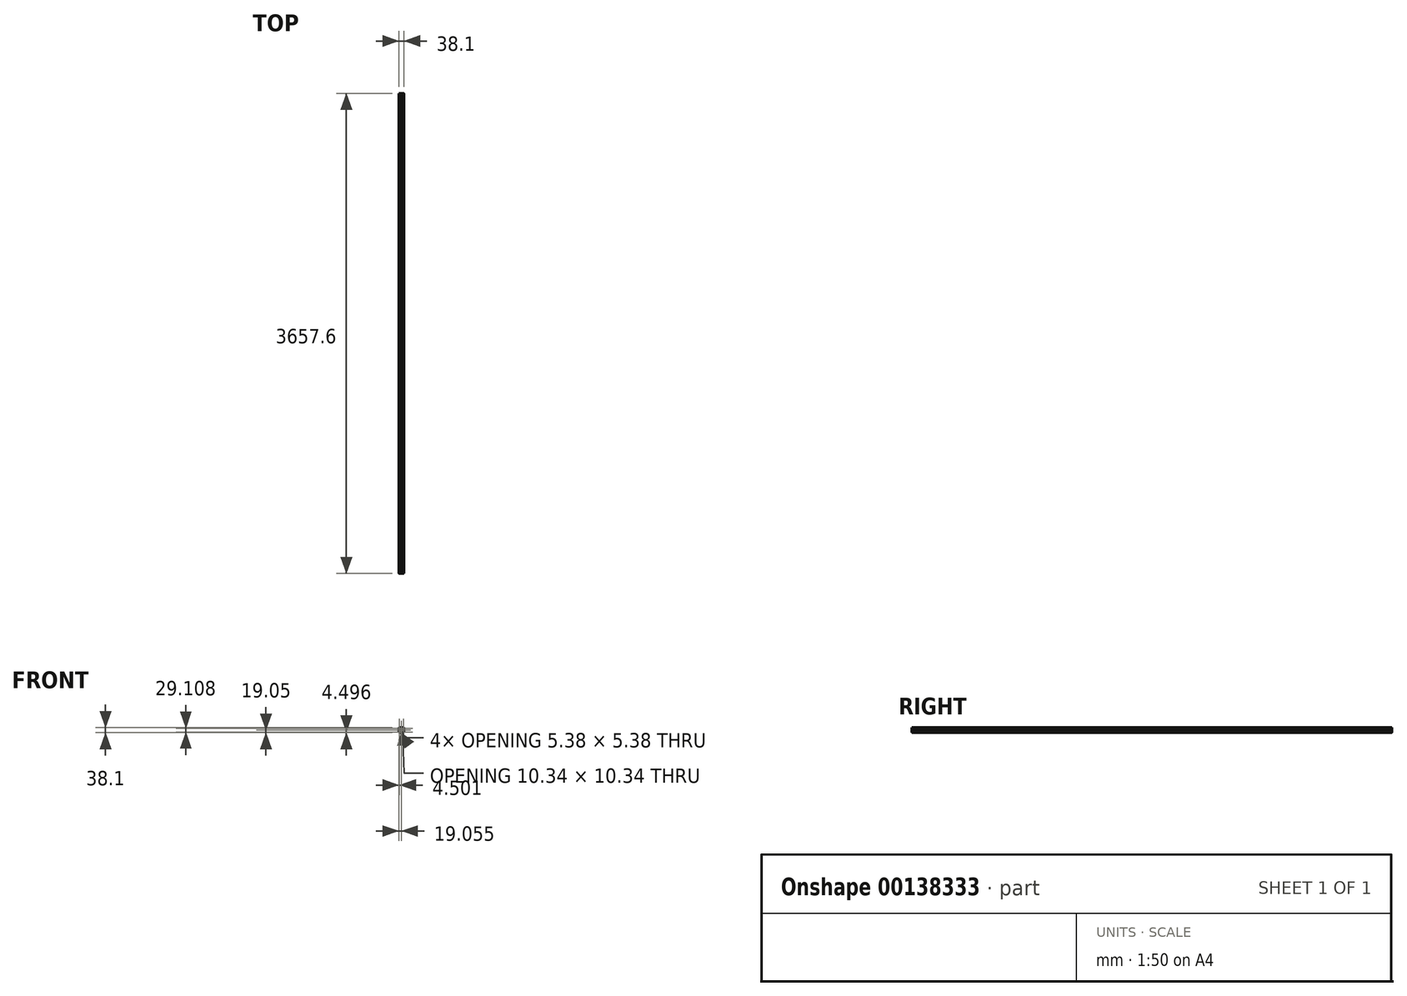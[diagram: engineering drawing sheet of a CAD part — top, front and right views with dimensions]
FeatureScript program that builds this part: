
annotation { "Feature Type Name" : "Feature", "Feature Type Description" : "" }
export const myFeature = defineFeature(function(context is Context, id is Id, definition is map)
    precondition{}
    {
        {
            var Q0;
            Q0=qCreatedBy(makeId("Front.planeOp"),FACE);
            var sketch = newSketch(context, id + "F0", { "sketchPlane" : qUnion([Q0])});
            skLineSegment(sketch, "E0", {"start": v(-126.4, 59.55) * mm, "end": v(-126.4, 54.72) * mm});
            skArc(sketch, "E1", {"start": v(-126.4, 53.2) * mm, "mid": v(-125.63, 53.96) * mm, "end": v(-126.4, 54.72) * mm});
            skArc(sketch, "E2", {"start": v(-126.4, 53.2) * mm, "mid": v(-125.47, 50.93) * mm, "end": v(-123.2, 50) * mm});
            skArc(sketch, "E3", {"start": v(-121.67, 50) * mm, "mid": v(-122.43, 50.76) * mm, "end": v(-123.2, 50) * mm});
            skLineSegment(sketch, "E4", {"start": v(-121.67, 50) * mm, "end": v(-116.84, 50) * mm});
            skArc(sketch, "E5", {"start": v(-115.32, 50) * mm, "mid": v(-116.08, 50.76) * mm, "end": v(-116.84, 50) * mm});
            skLineSegment(sketch, "E6", {"start": v(-115.32, 50) * mm, "end": v(-112.98, 50) * mm});
            skArc(sketch, "E7", {"start": v(-112.98, 50) * mm, "mid": v(-111.87, 50.46) * mm, "end": v(-111.4, 51.57) * mm});
            skLineSegment(sketch, "E8", {"start": v(-111.4, 51.57) * mm, "end": v(-111.4, 52.49) * mm});
            skArc(sketch, "E9", {"start": v(-111.4, 52.49) * mm, "mid": v(-111.87, 53.6) * mm, "end": v(-112.98, 54.06) * mm});
            skLineSegment(sketch, "E10", {"start": v(-112.98, 54.06) * mm, "end": v(-113.7, 54.06) * mm});
            skArc(sketch, "E11", {"start": v(-113.7, 54.06) * mm, "mid": v(-113.96, 53.95) * mm, "end": v(-114.08, 53.68) * mm});
            skLineSegment(sketch, "E12", {"start": v(-114.08, 53.68) * mm, "end": v(-114.08, 53.35) * mm});
            skArc(sketch, "E13", {"start": v(-114.46, 52.97) * mm, "mid": v(-114.19, 53.08) * mm, "end": v(-114.08, 53.35) * mm});
            skLineSegment(sketch, "E14", {"start": v(-114.46, 52.97) * mm, "end": v(-116.74, 52.97) * mm});
            skArc(sketch, "E15", {"start": v(-117.63, 53.86) * mm, "mid": v(-117.37, 53.23) * mm, "end": v(-116.74, 52.97) * mm});
            skLineSegment(sketch, "E16", {"start": v(-117.63, 53.86) * mm, "end": v(-117.63, 56.67) * mm});
            skArc(sketch, "E17", {"start": v(-117.26, 57.57) * mm, "mid": v(-117.54, 57.16) * mm, "end": v(-117.63, 56.67) * mm});
            skLineSegment(sketch, "E18", {"start": v(-117.26, 57.57) * mm, "end": v(-112.9, 61.93) * mm});
            skArc(sketch, "E19", {"start": v(-112, 62.3) * mm, "mid": v(-112.49, 62.2) * mm, "end": v(-112.9, 61.93) * mm});
            skLineSegment(sketch, "E20", {"start": v(-112, 62.3) * mm, "end": v(-102.7, 62.3) * mm});
            skArc(sketch, "E21", {"start": v(-101.8, 61.93) * mm, "mid": v(-102.2, 62.2) * mm, "end": v(-102.7, 62.3) * mm});
            skLineSegment(sketch, "E22", {"start": v(-101.8, 61.93) * mm, "end": v(-97.43, 57.57) * mm});
            skArc(sketch, "E23", {"start": v(-97.06, 56.67) * mm, "mid": v(-97.15, 57.16) * mm, "end": v(-97.43, 57.57) * mm});
            skLineSegment(sketch, "E24", {"start": v(-97.06, 56.67) * mm, "end": v(-97.06, 53.86) * mm});
            skArc(sketch, "E25", {"start": v(-97.95, 52.97) * mm, "mid": v(-97.32, 53.23) * mm, "end": v(-97.06, 53.86) * mm});
            skLineSegment(sketch, "E26", {"start": v(-97.95, 52.97) * mm, "end": v(-100.23, 52.97) * mm});
            skArc(sketch, "E27", {"start": v(-100.61, 53.35) * mm, "mid": v(-100.5, 53.08) * mm, "end": v(-100.23, 52.97) * mm});
            skLineSegment(sketch, "E28", {"start": v(-100.61, 53.35) * mm, "end": v(-100.61, 53.68) * mm});
            skArc(sketch, "E29", {"start": v(-100.61, 53.68) * mm, "mid": v(-100.73, 53.95) * mm, "end": v(-101, 54.06) * mm});
            skLineSegment(sketch, "E30", {"start": v(-101, 54.06) * mm, "end": v(-101.7, 54.06) * mm});
            skArc(sketch, "E31", {"start": v(-101.7, 54.06) * mm, "mid": v(-102.82, 53.6) * mm, "end": v(-103.28, 52.49) * mm});
            skLineSegment(sketch, "E32", {"start": v(-103.28, 52.49) * mm, "end": v(-103.28, 51.57) * mm});
            skArc(sketch, "E33", {"start": v(-103.28, 51.57) * mm, "mid": v(-102.82, 50.46) * mm, "end": v(-101.7, 50) * mm});
            skLineSegment(sketch, "E34", {"start": v(-101.7, 50) * mm, "end": v(-99.37, 50) * mm});
            skArc(sketch, "E35", {"start": v(-97.85, 50) * mm, "mid": v(-98.6, 50.76) * mm, "end": v(-99.37, 50) * mm});
            skLineSegment(sketch, "E36", {"start": v(-97.85, 50) * mm, "end": v(-93.02, 50) * mm});
            skArc(sketch, "E37", {"start": v(-91.5, 50) * mm, "mid": v(-92.26, 50.76) * mm, "end": v(-93.02, 50) * mm});
            skArc(sketch, "E38", {"start": v(-91.5, 50) * mm, "mid": v(-89.23, 50.93) * mm, "end": v(-88.3, 53.2) * mm});
            skArc(sketch, "E39", {"start": v(-88.3, 54.72) * mm, "mid": v(-89.06, 53.96) * mm, "end": v(-88.3, 53.2) * mm});
            skLineSegment(sketch, "E40", {"start": v(-88.3, 54.72) * mm, "end": v(-88.3, 59.55) * mm});
            skArc(sketch, "E41", {"start": v(-88.3, 61.07) * mm, "mid": v(-89.06, 60.31) * mm, "end": v(-88.3, 59.55) * mm});
            skLineSegment(sketch, "E42", {"start": v(-88.3, 61.07) * mm, "end": v(-88.3, 63.41) * mm});
            skArc(sketch, "E43", {"start": v(-88.3, 63.41) * mm, "mid": v(-88.76, 64.52) * mm, "end": v(-89.87, 64.99) * mm});
            skLineSegment(sketch, "E44", {"start": v(-89.87, 64.99) * mm, "end": v(-90.78, 64.99) * mm});
            skArc(sketch, "E45", {"start": v(-90.78, 64.99) * mm, "mid": v(-91.9, 64.52) * mm, "end": v(-92.36, 63.41) * mm});
            skLineSegment(sketch, "E46", {"start": v(-92.36, 63.41) * mm, "end": v(-92.36, 62.7) * mm});
            skArc(sketch, "E47", {"start": v(-92.36, 62.7) * mm, "mid": v(-92.25, 62.43) * mm, "end": v(-91.98, 62.32) * mm});
            skLineSegment(sketch, "E48", {"start": v(-91.98, 62.32) * mm, "end": v(-91.65, 62.32) * mm});
            skArc(sketch, "E49", {"start": v(-91.27, 61.94) * mm, "mid": v(-91.38, 62.2) * mm, "end": v(-91.65, 62.32) * mm});
            skLineSegment(sketch, "E50", {"start": v(-91.27, 61.94) * mm, "end": v(-91.27, 59.65) * mm});
            skArc(sketch, "E51", {"start": v(-92.16, 58.76) * mm, "mid": v(-91.53, 59.02) * mm, "end": v(-91.27, 59.65) * mm});
            skLineSegment(sketch, "E52", {"start": v(-92.16, 58.76) * mm, "end": v(-94.97, 58.76) * mm});
            skArc(sketch, "E53", {"start": v(-95.87, 59.13) * mm, "mid": v(-95.46, 58.86) * mm, "end": v(-94.97, 58.76) * mm});
            skLineSegment(sketch, "E54", {"start": v(-95.87, 59.13) * mm, "end": v(-100.23, 63.5) * mm});
            skArc(sketch, "E55", {"start": v(-100.6, 64.4) * mm, "mid": v(-100.5, 63.9) * mm, "end": v(-100.23, 63.5) * mm});
            skLineSegment(sketch, "E56", {"start": v(-100.6, 64.4) * mm, "end": v(-100.6, 73.7) * mm});
            skArc(sketch, "E57", {"start": v(-100.23, 74.6) * mm, "mid": v(-100.5, 74.2) * mm, "end": v(-100.6, 73.7) * mm});
            skLineSegment(sketch, "E58", {"start": v(-100.23, 74.6) * mm, "end": v(-95.87, 78.96) * mm});
            skArc(sketch, "E59", {"start": v(-94.97, 79.34) * mm, "mid": v(-95.46, 79.24) * mm, "end": v(-95.87, 78.96) * mm});
            skLineSegment(sketch, "E60", {"start": v(-94.97, 79.34) * mm, "end": v(-92.16, 79.34) * mm});
            skArc(sketch, "E61", {"start": v(-91.27, 78.45) * mm, "mid": v(-91.53, 79.08) * mm, "end": v(-92.16, 79.34) * mm});
            skLineSegment(sketch, "E62", {"start": v(-91.27, 78.45) * mm, "end": v(-91.27, 76.16) * mm});
            skArc(sketch, "E63", {"start": v(-91.65, 75.78) * mm, "mid": v(-91.38, 75.9) * mm, "end": v(-91.27, 76.16) * mm});
            skLineSegment(sketch, "E64", {"start": v(-91.65, 75.78) * mm, "end": v(-91.98, 75.78) * mm});
            skArc(sketch, "E65", {"start": v(-91.98, 75.78) * mm, "mid": v(-92.25, 75.67) * mm, "end": v(-92.36, 75.4) * mm});
            skLineSegment(sketch, "E66", {"start": v(-92.36, 75.4) * mm, "end": v(-92.36, 74.69) * mm});
            skArc(sketch, "E67", {"start": v(-92.36, 74.69) * mm, "mid": v(-91.9, 73.58) * mm, "end": v(-90.78, 73.11) * mm});
            skLineSegment(sketch, "E68", {"start": v(-90.78, 73.11) * mm, "end": v(-89.87, 73.11) * mm});
            skArc(sketch, "E69", {"start": v(-89.87, 73.11) * mm, "mid": v(-88.76, 73.58) * mm, "end": v(-88.3, 74.69) * mm});
            skLineSegment(sketch, "E70", {"start": v(-88.3, 74.69) * mm, "end": v(-88.3, 77.03) * mm});
            skArc(sketch, "E71", {"start": v(-88.3, 78.55) * mm, "mid": v(-89.06, 77.79) * mm, "end": v(-88.3, 77.03) * mm});
            skLineSegment(sketch, "E72", {"start": v(-88.3, 78.55) * mm, "end": v(-88.3, 83.38) * mm});
            skArc(sketch, "E73", {"start": v(-88.3, 84.9) * mm, "mid": v(-89.06, 84.14) * mm, "end": v(-88.3, 83.38) * mm});
            skArc(sketch, "E74", {"start": v(-88.3, 84.9) * mm, "mid": v(-89.23, 87.17) * mm, "end": v(-91.5, 88.1) * mm});
            skArc(sketch, "E75", {"start": v(-93.02, 88.1) * mm, "mid": v(-92.26, 87.34) * mm, "end": v(-91.5, 88.1) * mm});
            skLineSegment(sketch, "E76", {"start": v(-93.02, 88.1) * mm, "end": v(-97.85, 88.1) * mm});
            skArc(sketch, "E77", {"start": v(-99.37, 88.1) * mm, "mid": v(-98.6, 87.34) * mm, "end": v(-97.85, 88.1) * mm});
            skLineSegment(sketch, "E78", {"start": v(-99.37, 88.1) * mm, "end": v(-101.7, 88.1) * mm});
            skArc(sketch, "E79", {"start": v(-101.7, 88.1) * mm, "mid": v(-102.82, 87.64) * mm, "end": v(-103.28, 86.53) * mm});
            skLineSegment(sketch, "E80", {"start": v(-103.28, 86.53) * mm, "end": v(-103.28, 85.61) * mm});
            skArc(sketch, "E81", {"start": v(-103.28, 85.61) * mm, "mid": v(-102.82, 84.5) * mm, "end": v(-101.7, 84.04) * mm});
            skLineSegment(sketch, "E82", {"start": v(-101.7, 84.04) * mm, "end": v(-101, 84.04) * mm});
            skArc(sketch, "E83", {"start": v(-101, 84.04) * mm, "mid": v(-100.73, 84.15) * mm, "end": v(-100.61, 84.42) * mm});
            skLineSegment(sketch, "E84", {"start": v(-100.61, 84.42) * mm, "end": v(-100.61, 84.75) * mm});
            skArc(sketch, "E85", {"start": v(-100.23, 85.13) * mm, "mid": v(-100.5, 85.02) * mm, "end": v(-100.61, 84.75) * mm});
            skLineSegment(sketch, "E86", {"start": v(-100.23, 85.13) * mm, "end": v(-97.95, 85.13) * mm});
            skArc(sketch, "E87", {"start": v(-97.06, 84.24) * mm, "mid": v(-97.32, 84.87) * mm, "end": v(-97.95, 85.13) * mm});
            skLineSegment(sketch, "E88", {"start": v(-97.06, 84.24) * mm, "end": v(-97.06, 81.43) * mm});
            skArc(sketch, "E89", {"start": v(-97.43, 80.53) * mm, "mid": v(-97.15, 80.94) * mm, "end": v(-97.06, 81.43) * mm});
            skLineSegment(sketch, "E90", {"start": v(-97.43, 80.53) * mm, "end": v(-101.8, 76.17) * mm});
            skArc(sketch, "E91", {"start": v(-102.7, 75.8) * mm, "mid": v(-102.2, 75.9) * mm, "end": v(-101.8, 76.17) * mm});
            skLineSegment(sketch, "E92", {"start": v(-102.7, 75.8) * mm, "end": v(-112, 75.8) * mm});
            skArc(sketch, "E93", {"start": v(-112.9, 76.17) * mm, "mid": v(-112.49, 75.9) * mm, "end": v(-112, 75.8) * mm});
            skLineSegment(sketch, "E94", {"start": v(-112.9, 76.17) * mm, "end": v(-117.26, 80.53) * mm});
            skArc(sketch, "E95", {"start": v(-117.63, 81.43) * mm, "mid": v(-117.54, 80.94) * mm, "end": v(-117.26, 80.53) * mm});
            skLineSegment(sketch, "E96", {"start": v(-117.63, 81.43) * mm, "end": v(-117.63, 84.24) * mm});
            skArc(sketch, "E97", {"start": v(-116.74, 85.13) * mm, "mid": v(-117.37, 84.87) * mm, "end": v(-117.63, 84.24) * mm});
            skLineSegment(sketch, "E98", {"start": v(-116.74, 85.13) * mm, "end": v(-114.46, 85.13) * mm});
            skArc(sketch, "E99", {"start": v(-114.08, 84.75) * mm, "mid": v(-114.19, 85.02) * mm, "end": v(-114.46, 85.13) * mm});
            skLineSegment(sketch, "E100", {"start": v(-114.08, 84.75) * mm, "end": v(-114.08, 84.42) * mm});
            skArc(sketch, "E101", {"start": v(-114.08, 84.42) * mm, "mid": v(-113.96, 84.15) * mm, "end": v(-113.7, 84.04) * mm});
            skLineSegment(sketch, "E102", {"start": v(-113.7, 84.04) * mm, "end": v(-112.98, 84.04) * mm});
            skArc(sketch, "E103", {"start": v(-112.98, 84.04) * mm, "mid": v(-111.87, 84.5) * mm, "end": v(-111.4, 85.61) * mm});
            skLineSegment(sketch, "E104", {"start": v(-111.4, 85.61) * mm, "end": v(-111.4, 86.53) * mm});
            skArc(sketch, "E105", {"start": v(-111.4, 86.53) * mm, "mid": v(-111.87, 87.64) * mm, "end": v(-112.98, 88.1) * mm});
            skLineSegment(sketch, "E106", {"start": v(-112.98, 88.1) * mm, "end": v(-115.32, 88.1) * mm});
            skArc(sketch, "E107", {"start": v(-116.84, 88.1) * mm, "mid": v(-116.08, 87.34) * mm, "end": v(-115.32, 88.1) * mm});
            skLineSegment(sketch, "E108", {"start": v(-116.84, 88.1) * mm, "end": v(-121.67, 88.1) * mm});
            skArc(sketch, "E109", {"start": v(-123.2, 88.1) * mm, "mid": v(-122.43, 87.34) * mm, "end": v(-121.67, 88.1) * mm});
            skArc(sketch, "E110", {"start": v(-123.2, 88.1) * mm, "mid": v(-125.47, 87.17) * mm, "end": v(-126.4, 84.9) * mm});
            skArc(sketch, "E111", {"start": v(-126.4, 83.38) * mm, "mid": v(-125.63, 84.14) * mm, "end": v(-126.4, 84.9) * mm});
            skLineSegment(sketch, "E112", {"start": v(-126.4, 83.38) * mm, "end": v(-126.4, 78.55) * mm});
            skArc(sketch, "E113", {"start": v(-126.4, 77.03) * mm, "mid": v(-125.63, 77.79) * mm, "end": v(-126.4, 78.55) * mm});
            skLineSegment(sketch, "E114", {"start": v(-126.4, 77.03) * mm, "end": v(-126.4, 74.69) * mm});
            skArc(sketch, "E115", {"start": v(-126.4, 74.69) * mm, "mid": v(-125.93, 73.58) * mm, "end": v(-124.82, 73.11) * mm});
            skLineSegment(sketch, "E116", {"start": v(-124.82, 73.11) * mm, "end": v(-123.9, 73.11) * mm});
            skArc(sketch, "E117", {"start": v(-123.9, 73.11) * mm, "mid": v(-122.8, 73.58) * mm, "end": v(-122.33, 74.69) * mm});
            skLineSegment(sketch, "E118", {"start": v(-122.33, 74.69) * mm, "end": v(-122.33, 75.4) * mm});
            skArc(sketch, "E119", {"start": v(-122.33, 75.4) * mm, "mid": v(-122.44, 75.67) * mm, "end": v(-122.71, 75.78) * mm});
            skLineSegment(sketch, "E120", {"start": v(-122.71, 75.78) * mm, "end": v(-123.04, 75.78) * mm});
            skArc(sketch, "E121", {"start": v(-123.42, 76.16) * mm, "mid": v(-123.31, 75.9) * mm, "end": v(-123.04, 75.78) * mm});
            skLineSegment(sketch, "E122", {"start": v(-123.42, 76.16) * mm, "end": v(-123.42, 78.45) * mm});
            skArc(sketch, "E123", {"start": v(-122.53, 79.34) * mm, "mid": v(-123.16, 79.08) * mm, "end": v(-123.42, 78.45) * mm});
            skLineSegment(sketch, "E124", {"start": v(-122.53, 79.34) * mm, "end": v(-119.72, 79.34) * mm});
            skArc(sketch, "E125", {"start": v(-118.82, 78.96) * mm, "mid": v(-119.23, 79.24) * mm, "end": v(-119.72, 79.34) * mm});
            skLineSegment(sketch, "E126", {"start": v(-118.82, 78.96) * mm, "end": v(-114.46, 74.6) * mm});
            skArc(sketch, "E127", {"start": v(-114.09, 73.7) * mm, "mid": v(-114.19, 74.2) * mm, "end": v(-114.46, 74.6) * mm});
            skLineSegment(sketch, "E128", {"start": v(-114.09, 73.7) * mm, "end": v(-114.09, 64.4) * mm});
            skArc(sketch, "E129", {"start": v(-114.46, 63.5) * mm, "mid": v(-114.19, 63.9) * mm, "end": v(-114.09, 64.4) * mm});
            skLineSegment(sketch, "E130", {"start": v(-114.46, 63.5) * mm, "end": v(-118.82, 59.13) * mm});
            skArc(sketch, "E131", {"start": v(-119.72, 58.76) * mm, "mid": v(-119.23, 58.86) * mm, "end": v(-118.82, 59.13) * mm});
            skLineSegment(sketch, "E132", {"start": v(-119.72, 58.76) * mm, "end": v(-122.53, 58.76) * mm});
            skArc(sketch, "E133", {"start": v(-123.42, 59.65) * mm, "mid": v(-123.16, 59.02) * mm, "end": v(-122.53, 58.76) * mm});
            skLineSegment(sketch, "E134", {"start": v(-123.42, 59.65) * mm, "end": v(-123.42, 61.94) * mm});
            skArc(sketch, "E135", {"start": v(-123.04, 62.32) * mm, "mid": v(-123.31, 62.2) * mm, "end": v(-123.42, 61.94) * mm});
            skLineSegment(sketch, "E136", {"start": v(-123.04, 62.32) * mm, "end": v(-122.71, 62.32) * mm});
            skArc(sketch, "E137", {"start": v(-122.71, 62.32) * mm, "mid": v(-122.44, 62.43) * mm, "end": v(-122.33, 62.7) * mm});
            skLineSegment(sketch, "E138", {"start": v(-122.33, 62.7) * mm, "end": v(-122.33, 63.41) * mm});
            skArc(sketch, "E139", {"start": v(-122.33, 63.41) * mm, "mid": v(-122.8, 64.52) * mm, "end": v(-123.9, 64.99) * mm});
            skLineSegment(sketch, "E140", {"start": v(-123.9, 64.99) * mm, "end": v(-124.82, 64.99) * mm});
            skArc(sketch, "E141", {"start": v(-124.82, 64.99) * mm, "mid": v(-125.93, 64.52) * mm, "end": v(-126.4, 63.41) * mm});
            skLineSegment(sketch, "E142", {"start": v(-126.4, 63.41) * mm, "end": v(-126.4, 61.07) * mm});
            skArc(sketch, "E143", {"start": v(-95.1, 86.3) * mm, "mid": v(-95.37, 86.18) * mm, "end": v(-95.48, 85.92) * mm});
            skLineSegment(sketch, "E144", {"start": v(-92.9, 86.3) * mm, "end": v(-95.1, 86.3) * mm});
            skArc(sketch, "E145", {"start": v(-90.1, 83.5) * mm, "mid": v(-90.92, 85.48) * mm, "end": v(-92.9, 86.3) * mm});
            skLineSegment(sketch, "E146", {"start": v(-90.1, 81.3) * mm, "end": v(-90.1, 83.5) * mm});
            skArc(sketch, "E147", {"start": v(-90.48, 80.91) * mm, "mid": v(-90.21, 81.02) * mm, "end": v(-90.1, 81.3) * mm});
            skLineSegment(sketch, "E148", {"start": v(-92.25, 80.91) * mm, "end": v(-90.48, 80.91) * mm});
            skLineSegment(sketch, "E149", {"start": v(-92.8, 81.45) * mm, "end": v(-92.25, 80.91) * mm});
            skLineSegment(sketch, "E150", {"start": v(-93.33, 80.91) * mm, "end": v(-92.8, 81.45) * mm});
            skLineSegment(sketch, "E151", {"start": v(-95.1, 80.91) * mm, "end": v(-93.33, 80.91) * mm});
            skArc(sketch, "E152", {"start": v(-95.48, 81.3) * mm, "mid": v(-95.37, 81.02) * mm, "end": v(-95.1, 80.91) * mm});
            skLineSegment(sketch, "E153", {"start": v(-95.48, 83.07) * mm, "end": v(-95.48, 81.3) * mm});
            skLineSegment(sketch, "E154", {"start": v(-94.94, 83.6) * mm, "end": v(-95.48, 83.07) * mm});
            skLineSegment(sketch, "E155", {"start": v(-95.48, 84.14) * mm, "end": v(-94.94, 83.6) * mm});
            skLineSegment(sketch, "E156", {"start": v(-95.48, 56.8) * mm, "end": v(-95.48, 55.03) * mm});
            skArc(sketch, "E157", {"start": v(-95.1, 57.19) * mm, "mid": v(-95.37, 57.08) * mm, "end": v(-95.48, 56.8) * mm});
            skLineSegment(sketch, "E158", {"start": v(-93.33, 57.19) * mm, "end": v(-95.1, 57.19) * mm});
            skLineSegment(sketch, "E159", {"start": v(-92.8, 56.65) * mm, "end": v(-93.33, 57.19) * mm});
            skLineSegment(sketch, "E160", {"start": v(-92.25, 57.19) * mm, "end": v(-92.8, 56.65) * mm});
            skLineSegment(sketch, "E161", {"start": v(-90.48, 57.19) * mm, "end": v(-92.25, 57.19) * mm});
            skArc(sketch, "E162", {"start": v(-90.1, 56.8) * mm, "mid": v(-90.21, 57.08) * mm, "end": v(-90.48, 57.19) * mm});
            skLineSegment(sketch, "E163", {"start": v(-90.1, 54.6) * mm, "end": v(-90.1, 56.8) * mm});
            skArc(sketch, "E164", {"start": v(-92.9, 51.8) * mm, "mid": v(-90.92, 52.62) * mm, "end": v(-90.1, 54.6) * mm});
            skLineSegment(sketch, "E165", {"start": v(-95.1, 51.8) * mm, "end": v(-92.9, 51.8) * mm});
            skArc(sketch, "E166", {"start": v(-95.48, 52.18) * mm, "mid": v(-95.37, 51.91) * mm, "end": v(-95.1, 51.8) * mm});
            skLineSegment(sketch, "E167", {"start": v(-95.48, 53.96) * mm, "end": v(-95.48, 52.18) * mm});
            skLineSegment(sketch, "E168", {"start": v(-94.94, 54.5) * mm, "end": v(-95.48, 53.96) * mm});
            skLineSegment(sketch, "E169", {"start": v(-112.51, 65.13) * mm, "end": v(-112.51, 64.14) * mm});
            skArc(sketch, "E170", {"start": v(-112.25, 65.76) * mm, "mid": v(-112.45, 65.47) * mm, "end": v(-112.51, 65.13) * mm});
            skLineSegment(sketch, "E171", {"start": v(-110.54, 67.47) * mm, "end": v(-112.25, 65.76) * mm});
            skArc(sketch, "E172", {"start": v(-110.54, 67.47) * mm, "mid": v(-110.44, 67.66) * mm, "end": v(-110.46, 67.87) * mm});
            skArc(sketch, "E173", {"start": v(-110.46, 70.23) * mm, "mid": v(-110.67, 69.05) * mm, "end": v(-110.46, 67.87) * mm});
            skArc(sketch, "E174", {"start": v(-110.46, 70.23) * mm, "mid": v(-110.44, 70.44) * mm, "end": v(-110.54, 70.63) * mm});
            skLineSegment(sketch, "E175", {"start": v(-112.25, 72.34) * mm, "end": v(-110.54, 70.63) * mm});
            skArc(sketch, "E176", {"start": v(-112.51, 72.97) * mm, "mid": v(-112.45, 72.63) * mm, "end": v(-112.25, 72.34) * mm});
            skLineSegment(sketch, "E177", {"start": v(-112.51, 73.96) * mm, "end": v(-112.51, 72.97) * mm});
            skArc(sketch, "E178", {"start": v(-112.26, 74.22) * mm, "mid": v(-112.44, 74.14) * mm, "end": v(-112.51, 73.96) * mm});
            skLineSegment(sketch, "E179", {"start": v(-111.27, 74.22) * mm, "end": v(-112.26, 74.22) * mm});
            skArc(sketch, "E180", {"start": v(-110.64, 73.96) * mm, "mid": v(-110.93, 74.15) * mm, "end": v(-111.27, 74.22) * mm});
            skLineSegment(sketch, "E181", {"start": v(-108.93, 72.25) * mm, "end": v(-110.64, 73.96) * mm});
            skArc(sketch, "E182", {"start": v(-108.93, 72.25) * mm, "mid": v(-108.74, 72.15) * mm, "end": v(-108.52, 72.16) * mm});
            skArc(sketch, "E183", {"start": v(-106.17, 72.16) * mm, "mid": v(-107.35, 72.38) * mm, "end": v(-108.52, 72.16) * mm});
            skArc(sketch, "E184", {"start": v(-106.17, 72.16) * mm, "mid": v(-105.95, 72.15) * mm, "end": v(-105.76, 72.25) * mm});
            skLineSegment(sketch, "E185", {"start": v(-104.05, 73.96) * mm, "end": v(-105.76, 72.25) * mm});
            skArc(sketch, "E186", {"start": v(-103.42, 74.22) * mm, "mid": v(-103.76, 74.15) * mm, "end": v(-104.05, 73.96) * mm});
            skLineSegment(sketch, "E187", {"start": v(-102.43, 74.22) * mm, "end": v(-103.42, 74.22) * mm});
            skArc(sketch, "E188", {"start": v(-102.18, 73.96) * mm, "mid": v(-102.25, 74.14) * mm, "end": v(-102.43, 74.22) * mm});
            skLineSegment(sketch, "E189", {"start": v(-102.18, 72.97) * mm, "end": v(-102.18, 73.96) * mm});
            skArc(sketch, "E190", {"start": v(-102.44, 72.34) * mm, "mid": v(-102.24, 72.63) * mm, "end": v(-102.18, 72.97) * mm});
            skLineSegment(sketch, "E191", {"start": v(-104.15, 70.63) * mm, "end": v(-102.44, 72.34) * mm});
            skArc(sketch, "E192", {"start": v(-104.15, 70.63) * mm, "mid": v(-104.25, 70.44) * mm, "end": v(-104.23, 70.23) * mm});
            skArc(sketch, "E193", {"start": v(-104.23, 67.87) * mm, "mid": v(-104.02, 69.05) * mm, "end": v(-104.23, 70.23) * mm});
            skArc(sketch, "E194", {"start": v(-104.23, 67.87) * mm, "mid": v(-104.25, 67.66) * mm, "end": v(-104.15, 67.47) * mm});
            skLineSegment(sketch, "E195", {"start": v(-102.44, 65.76) * mm, "end": v(-104.15, 67.47) * mm});
            skArc(sketch, "E196", {"start": v(-102.18, 65.13) * mm, "mid": v(-102.24, 65.47) * mm, "end": v(-102.44, 65.76) * mm});
            skLineSegment(sketch, "E197", {"start": v(-102.18, 64.14) * mm, "end": v(-102.18, 65.13) * mm});
            skArc(sketch, "E198", {"start": v(-102.43, 63.88) * mm, "mid": v(-102.25, 63.96) * mm, "end": v(-102.18, 64.14) * mm});
            skLineSegment(sketch, "E199", {"start": v(-103.42, 63.88) * mm, "end": v(-102.43, 63.88) * mm});
            skArc(sketch, "E200", {"start": v(-104.05, 64.14) * mm, "mid": v(-103.76, 63.95) * mm, "end": v(-103.42, 63.88) * mm});
            skLineSegment(sketch, "E201", {"start": v(-105.76, 65.85) * mm, "end": v(-104.05, 64.14) * mm});
            skArc(sketch, "E202", {"start": v(-105.76, 65.85) * mm, "mid": v(-105.95, 65.95) * mm, "end": v(-106.17, 65.94) * mm});
            skArc(sketch, "E203", {"start": v(-108.52, 65.94) * mm, "mid": v(-107.35, 65.72) * mm, "end": v(-106.17, 65.94) * mm});
            skArc(sketch, "E204", {"start": v(-108.52, 65.94) * mm, "mid": v(-108.74, 65.95) * mm, "end": v(-108.93, 65.85) * mm});
            skLineSegment(sketch, "E205", {"start": v(-110.64, 64.14) * mm, "end": v(-108.93, 65.85) * mm});
            skArc(sketch, "E206", {"start": v(-111.27, 63.88) * mm, "mid": v(-110.93, 63.95) * mm, "end": v(-110.64, 64.14) * mm});
            skLineSegment(sketch, "E207", {"start": v(-112.26, 63.88) * mm, "end": v(-111.27, 63.88) * mm});
            skLineSegment(sketch, "E208", {"start": v(-124.6, 56.8) * mm, "end": v(-124.6, 54.6) * mm});
            skArc(sketch, "E209", {"start": v(-124.21, 57.19) * mm, "mid": v(-124.48, 57.08) * mm, "end": v(-124.6, 56.8) * mm});
            skLineSegment(sketch, "E210", {"start": v(-122.44, 57.19) * mm, "end": v(-124.21, 57.19) * mm});
            skLineSegment(sketch, "E211", {"start": v(-121.9, 56.65) * mm, "end": v(-122.44, 57.19) * mm});
            skLineSegment(sketch, "E212", {"start": v(-121.36, 57.19) * mm, "end": v(-121.9, 56.65) * mm});
            skLineSegment(sketch, "E213", {"start": v(-119.59, 57.19) * mm, "end": v(-121.36, 57.19) * mm});
            skArc(sketch, "E214", {"start": v(-119.2, 56.8) * mm, "mid": v(-119.32, 57.08) * mm, "end": v(-119.59, 57.19) * mm});
            skLineSegment(sketch, "E215", {"start": v(-119.2, 55.03) * mm, "end": v(-119.2, 56.8) * mm});
            skLineSegment(sketch, "E216", {"start": v(-119.75, 54.5) * mm, "end": v(-119.2, 55.03) * mm});
            skLineSegment(sketch, "E217", {"start": v(-119.2, 53.96) * mm, "end": v(-119.75, 54.5) * mm});
            skLineSegment(sketch, "E218", {"start": v(-119.2, 52.18) * mm, "end": v(-119.2, 53.96) * mm});
            skArc(sketch, "E219", {"start": v(-119.59, 51.8) * mm, "mid": v(-119.32, 51.91) * mm, "end": v(-119.2, 52.18) * mm});
            skLineSegment(sketch, "E220", {"start": v(-121.8, 51.8) * mm, "end": v(-119.59, 51.8) * mm});
            skLineSegment(sketch, "E221", {"start": v(-124.6, 83.5) * mm, "end": v(-124.6, 81.3) * mm});
            skArc(sketch, "E222", {"start": v(-121.8, 86.3) * mm, "mid": v(-123.77, 85.48) * mm, "end": v(-124.6, 83.5) * mm});
            skLineSegment(sketch, "E223", {"start": v(-119.59, 86.3) * mm, "end": v(-121.8, 86.3) * mm});
            skArc(sketch, "E224", {"start": v(-119.2, 85.92) * mm, "mid": v(-119.32, 86.18) * mm, "end": v(-119.59, 86.3) * mm});
            skLineSegment(sketch, "E225", {"start": v(-119.2, 84.14) * mm, "end": v(-119.2, 85.92) * mm});
            skLineSegment(sketch, "E226", {"start": v(-119.75, 83.6) * mm, "end": v(-119.2, 84.14) * mm});
            skLineSegment(sketch, "E227", {"start": v(-119.2, 83.07) * mm, "end": v(-119.75, 83.6) * mm});
            skLineSegment(sketch, "E228", {"start": v(-119.2, 81.3) * mm, "end": v(-119.2, 83.07) * mm});
            skArc(sketch, "E229", {"start": v(-119.59, 80.91) * mm, "mid": v(-119.32, 81.02) * mm, "end": v(-119.2, 81.3) * mm});
            skLineSegment(sketch, "E230", {"start": v(-121.36, 80.91) * mm, "end": v(-119.59, 80.91) * mm});
            skLineSegment(sketch, "E231", {"start": v(-121.9, 81.45) * mm, "end": v(-121.36, 80.91) * mm});
            skLineSegment(sketch, "E232", {"start": v(-122.44, 80.91) * mm, "end": v(-121.9, 81.45) * mm});
            skLineSegment(sketch, "E233", {"start": v(-124.21, 80.91) * mm, "end": v(-122.44, 80.91) * mm});
            skLineSegment(sketch, "E234", {"start": v(-95.48, 85.92) * mm, "end": v(-95.48, 84.14) * mm});
            skLineSegment(sketch, "E235", {"start": v(-95.48, 55.03) * mm, "end": v(-94.94, 54.5) * mm});
            skArc(sketch, "E236", {"start": v(-112.51, 64.14) * mm, "mid": v(-112.44, 63.96) * mm, "end": v(-112.26, 63.88) * mm});
            skArc(sketch, "E237", {"start": v(-124.6, 54.6) * mm, "mid": v(-123.77, 52.62) * mm, "end": v(-121.8, 51.8) * mm});
            skArc(sketch, "E238", {"start": v(-124.6, 81.3) * mm, "mid": v(-124.48, 81.02) * mm, "end": v(-124.21, 80.91) * mm});
            skArc(sketch, "E239", {"start": v(-126.4, 59.55) * mm, "mid": v(-125.63, 60.31) * mm, "end": v(-126.4, 61.07) * mm});
            skSolve(sketch);
        }
        {
            var Q0;
            Q0=makeQuery(id+"F0.imprint","IMPRINT",FACE,{"disambiguationData":[TD([[makeQuery(id+"F0.imprint","IMPRINT",EDGE,{"derivedFrom":sQuery(id+"F0.wireOp",EDGE,"E0")}),1.0]])]});
            extrude(context, id + "F1", {"entities" : qUnion([Q0]), "endBound" : BoundingType.SYMMETRIC, "depth" : 3657.6 * mm});
        }
    });
